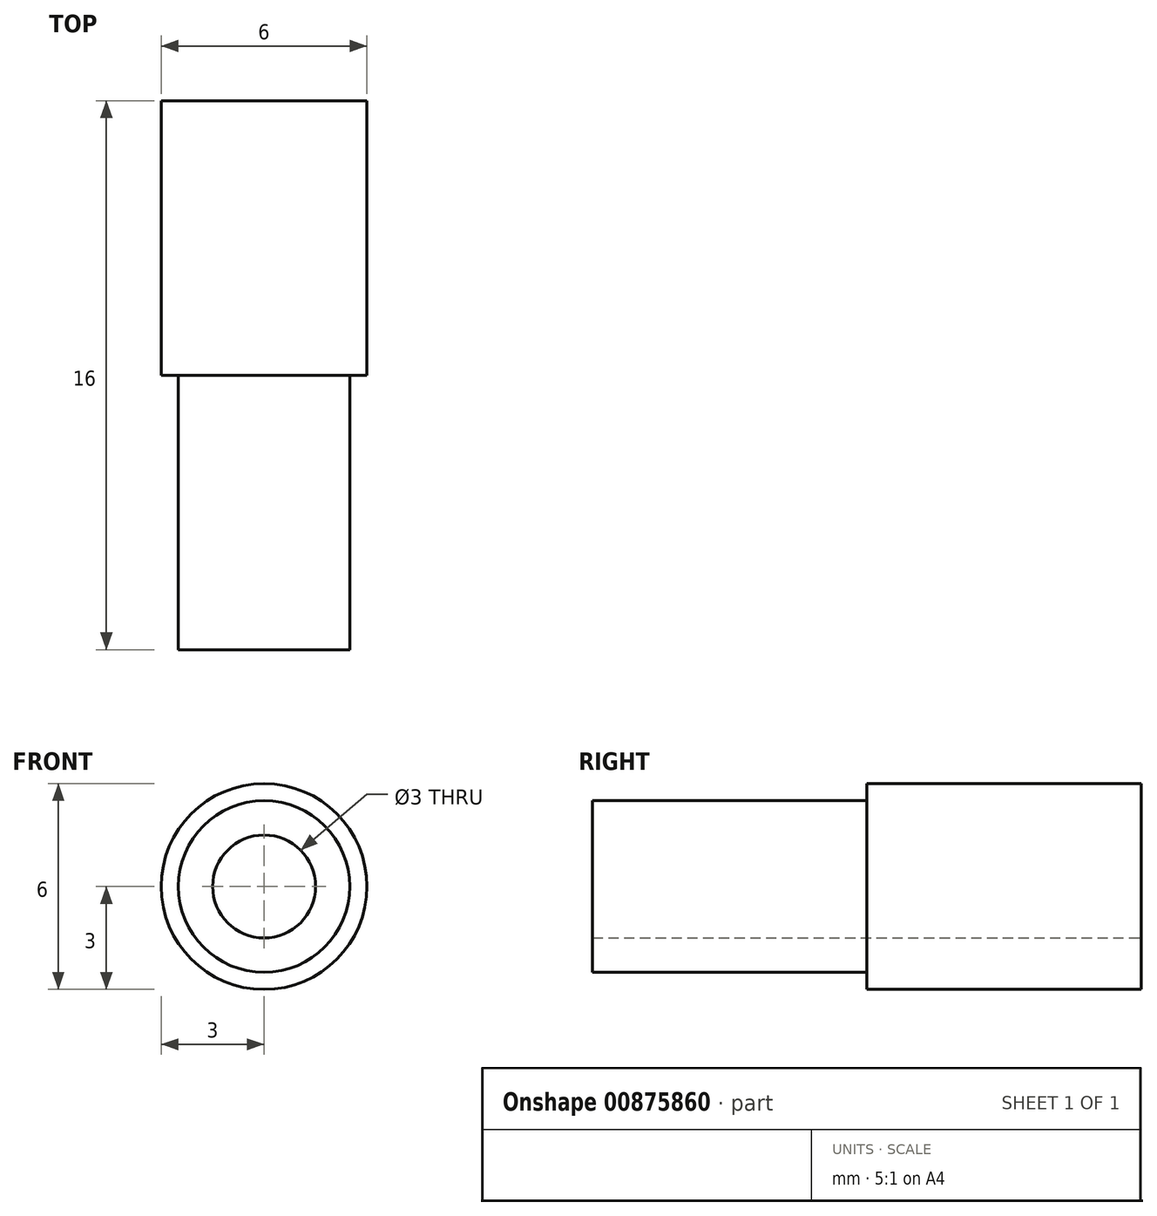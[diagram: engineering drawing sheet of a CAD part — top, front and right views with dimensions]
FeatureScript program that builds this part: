
annotation { "Feature Type Name" : "Feature", "Feature Type Description" : "" }
export const myFeature = defineFeature(function(context is Context, id is Id, definition is map)
    precondition{}
    {
        {
            var Q0;
            Q0=qCreatedBy(makeId("Front.planeOp"),FACE);
            var sketch = newSketch(context, id + "F0", { "sketchPlane" : qUnion([Q0])});
            skCircle(sketch, "E0", {"center": v(0, 0) * mm, "radius": 3 * mm});
            skSolve(sketch);
        }
        {
            var Q0;
            Q0 = qSketchRegion(id + "F0", true);
            extrude(context, id + "F1", {"entities" : qUnion([Q0]), "depth" : 8 * mm, "offsetDistance" : 25 * mm});
        }
        {
            var Q0;
            Q0=qCreatedBy(makeId("Front.planeOp"),FACE);
            var sketch = newSketch(context, id + "F2", { "sketchPlane" : qUnion([Q0])});
            skCircle(sketch, "E1", {"center": v(0, 0) * mm, "radius": 2.5 * mm});
            skSolve(sketch);
        }
        {
            var Q0;
            Q0 = qSketchRegion(id + "F2", true);
            extrude(context, id + "F3", {"entities" : qUnion([Q0]), "operationType" : NewBodyOperationType.ADD, "depth" : 16 * mm, "offsetDistance" : 25 * mm});
        }
        {
            var Q0;
            Q0=qCreatedBy(makeId("Front.planeOp"),FACE);
            var sketch = newSketch(context, id + "F4", { "sketchPlane" : qUnion([Q0])});
            skCircle(sketch, "E2", {"center": v(0, 0) * mm, "radius": 1.5 * mm});
            skSolve(sketch);
        }
        {
            var Q0;
            Q0 = qSketchRegion(id + "F4", true);
            extrude(context, id + "F5", {"entities" : qUnion([Q0]), "operationType" : NewBodyOperationType.REMOVE, "depth" : 16 * mm, "offsetDistance" : 25 * mm});
        }
    });
